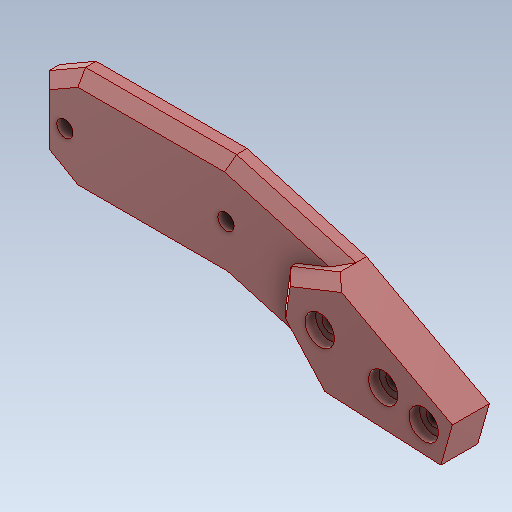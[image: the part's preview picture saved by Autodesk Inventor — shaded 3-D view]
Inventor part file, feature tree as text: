
AUTODESK INVENTOR PART (.ipt)
format: ipt  version: 2020 (Build 240168000, 168)  size: 157,696 bytes
history: native  units: in
note: dims shown in document units (in); Inventor stores cm internally (conversion verified against a paired STEP export)
features: other x3, sketch x3
ambient origin geometry x8: Origin, YZ Plane, XZ Plane, XY Plane, X Axis, Y Axis, Z Axis, Center Point
bodies: Solid1 (feature_tree)
feature tree (6):
  other  "Fibula.ipt"
  other  "Solid1::Fibula.ipt"
  other  "TaggingFeature1"
  sketch  "Sketch1"  dims[d0=0.3937in]
  sketch  "Sketch3"
  sketch  "Sketch4"
